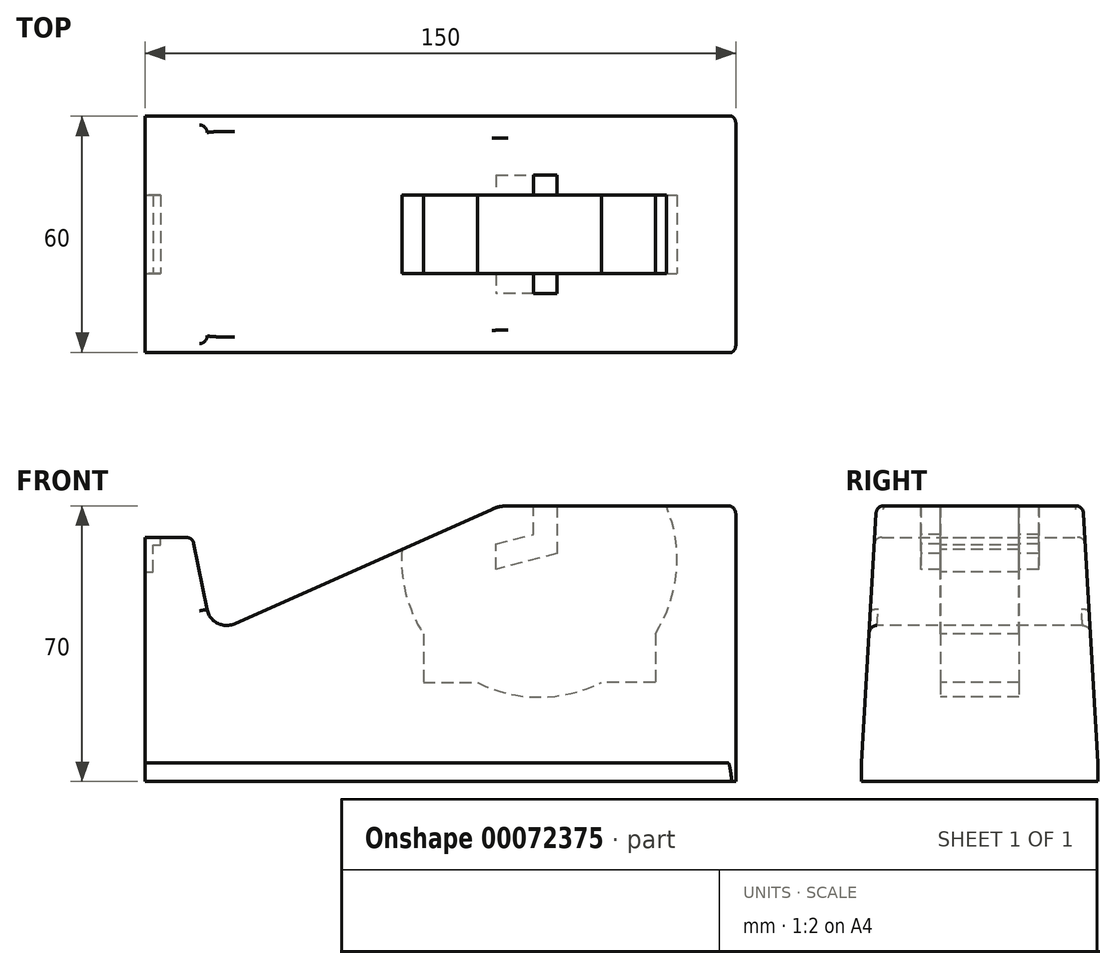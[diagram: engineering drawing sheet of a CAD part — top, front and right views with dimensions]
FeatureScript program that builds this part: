
annotation { "Feature Type Name" : "Feature", "Feature Type Description" : "" }
export const myFeature = defineFeature(function(context is Context, id is Id, definition is map)
    precondition{}
    {
        {
            var Q0;
            Q0=qCreatedBy(makeId("Front.planeOp"),FACE);
            var sketch = newSketch(context, id + "F0", { "sketchPlane" : qUnion([Q0])});
            skLineSegment(sketch, "E0", {"start": v(0, 0) * mm, "end": v(150, 0) * mm});
            skLineSegment(sketch, "E1", {"start": v(150, 0) * mm, "end": v(150, 70) * mm});
            skLineSegment(sketch, "E2", {"start": v(150, 70) * mm, "end": v(90, 70) * mm});
            skLineSegment(sketch, "E3", {"start": v(0, 62) * mm, "end": v(0, 0) * mm});
            skLineSegment(sketch, "E4", {"start": v(0, 62) * mm, "end": v(12, 62) * mm});
            skLineSegment(sketch, "E5", {"start": v(12, 62) * mm, "end": v(16.95, 37.5) * mm});
            skLineSegment(sketch, "E6", {"start": v(16.95, 37.5) * mm, "end": v(90, 70) * mm});
            skSolve(sketch);
        }
        {
            var Q0;
            Q0 = qSketchRegion(id + "F0", true);
            extrude(context, id + "F1", {"entities" : qUnion([Q0]), "depth" : 60 * mm, "symmetric" : true});
        }
        {
            var Q0;
            Q0=qCreatedBy(makeId("Front.planeOp"),FACE);
            var sketch = newSketch(context, id + "F2", { "sketchPlane" : qUnion([Q0])});
            skCircle(sketch, "E7", {"center": v(100.1, 56.39) * mm, "radius": 35 * mm});
            skLineSegment(sketch, "E8", {"start": v(0, 53.2) * mm, "end": v(1.94, 53.2) * mm});
            skLineSegment(sketch, "E9", {"start": v(1.94, 53.2) * mm, "end": v(1.94, 60) * mm});
            skLineSegment(sketch, "E10", {"start": v(1.94, 60) * mm, "end": v(3.89, 60) * mm});
            skLineSegment(sketch, "E11", {"start": v(3.89, 60) * mm, "end": v(3.89, 61.8) * mm});
            skLineSegment(sketch, "E12", {"start": v(3.89, 61.8) * mm, "end": v(0, 61.8) * mm});
            skLineSegment(sketch, "E13", {"start": v(0, 61.8) * mm, "end": v(0, 53.2) * mm});
            skLineSegment(sketch, "E14", {"start": v(70.65, 37.48) * mm, "end": v(70.65, 25.12) * mm});
            skLineSegment(sketch, "E15", {"start": v(129.55, 37.48) * mm, "end": v(129.55, 25.12) * mm});
            skLineSegment(sketch, "E16", {"start": v(70.65, 25.12) * mm, "end": v(84.36, 25.12) * mm});
            skLineSegment(sketch, "E17", {"start": v(129.55, 25.12) * mm, "end": v(115.84, 25.12) * mm});
            skSolve(sketch);
        }
        {
            var Q0;
            Q0 = qSketchRegion(id + "F2", true);
            extrude(context, id + "F3", {"entities" : qUnion([Q0]), "operationType" : NewBodyOperationType.REMOVE, "oppositeDirection" : true, "depth" : 20 * mm, "symmetric" : true});
        }
        {
            var Q0;
            Q0=qCreatedBy(makeId("Front.planeOp"),FACE);
            var sketch = newSketch(context, id + "F4", { "sketchPlane" : qUnion([Q0])});
            skLineSegment(sketch, "E18", {"start": v(104.65, 70.19) * mm, "end": v(104.65, 57.84) * mm});
            skLineSegment(sketch, "E19", {"start": v(104.65, 57.84) * mm, "end": v(89.14, 53.9) * mm});
            skLineSegment(sketch, "E20", {"start": v(89.14, 53.9) * mm, "end": v(89.14, 60.37) * mm});
            skLineSegment(sketch, "E21", {"start": v(89.14, 60.37) * mm, "end": v(98.65, 62.79) * mm});
            skLineSegment(sketch, "E22", {"start": v(98.65, 62.79) * mm, "end": v(98.65, 70.19) * mm});
            skLineSegment(sketch, "E23", {"start": v(104.65, 70.19) * mm, "end": v(98.65, 70.19) * mm});
            skSolve(sketch);
        }
        {
            var Q0;
            Q0 = qSketchRegion(id + "F4", true);
            extrude(context, id + "F5", {"entities" : qUnion([Q0]), "operationType" : NewBodyOperationType.REMOVE, "oppositeDirection" : true, "depth" : 30 * mm, "symmetric" : true});
        }
        {
            var Q0;
            Q0=qCreatedBy(makeId("Right.planeOp"),FACE);
            var sketch = newSketch(context, id + "F6", { "sketchPlane" : qUnion([Q0])});
            skLineSegment(sketch, "E24", {"start": v(30.27, 0) * mm, "end": v(25.6, 81.55) * mm});
            skLineSegment(sketch, "E25", {"start": v(25.6, 81.55) * mm, "end": v(45.78, 81.36) * mm});
            skLineSegment(sketch, "E26", {"start": v(45.78, 81.36) * mm, "end": v(30.27, 0) * mm});
            skLineSegment(sketch, "E27.MirrorCS", {"start": v(-25.6, 81.55) * mm, "end": v(-45.78, 81.36) * mm});
            skLineSegment(sketch, "E28.MirrorCS", {"start": v(-30.27, 0) * mm, "end": v(-25.6, 81.55) * mm});
            skLineSegment(sketch, "E29.MirrorCS", {"start": v(-45.78, 81.36) * mm, "end": v(-30.27, 0) * mm});
            skSolve(sketch);
        }
        {
            var Q0;
            Q0 = qSketchRegion(id + "F6", true);
            extrude(context, id + "F7", {"entities" : qUnion([Q0]), "operationType" : NewBodyOperationType.REMOVE, "endBound" : BoundingType.THROUGH_ALL, "depth" : 27.02 * mm});
        }
        {
            var Q0;
            Q0=makeQuery(id+"F1.opExtrude","SWEPT_EDGE",EDGE,{"disambiguationData":[OSD([sQuery(id+"F0.wireOp",EDGE,"E5"),sQuery(id+"F0.wireOp",EDGE,"E6")])]});
            fillet(context, id + "F8", {"entities" : qUnion([Q0]), "radius" : 5 * mm, "tangentPropagation" : true, "allowEdgeOverflow" : false});
        }
        {
            var Q0;
            Q0=makeQuery(id+"F1.opExtrude","SWEPT_EDGE",EDGE,{"disambiguationData":[OSD([sQuery(id+"F0.wireOp",EDGE,"E4"),sQuery(id+"F0.wireOp",EDGE,"E5")])]});
            var Q1;
            Q1=makeQuery(id+"F7.boolean.opBoolean","INTERSECT",EDGE,{"derivedFrom":[makeQuery(id+"F1.opExtrude","SWEPT_FACE",FACE,{"disambiguationData":[OSD([sQuery(id+"F0.wireOp",EDGE,"E6")])]}),makeQuery(id+"F7.opExtrude","SWEPT_FACE",FACE,{"disambiguationData":[OSD([sQuery(id+"F6.wireOp",EDGE,"E28.MirrorCS")])]})]});
            var Q2;
            Q2=makeQuery(id+"F7.boolean.opBoolean","INTERSECT",EDGE,{"derivedFrom":[makeQuery(id+"F1.opExtrude","SWEPT_FACE",FACE,{"disambiguationData":[OSD([sQuery(id+"F0.wireOp",EDGE,"E2")])]}),makeQuery(id+"F7.opExtrude","SWEPT_FACE",FACE,{"disambiguationData":[OSD([sQuery(id+"F6.wireOp",EDGE,"E28.MirrorCS")])]})]});
            var Q3;
            Q3=makeQuery(id+"F7.boolean.opBoolean","INTERSECT",EDGE,{"derivedFrom":[makeQuery(id+"F1.opExtrude","SWEPT_FACE",FACE,{"disambiguationData":[OSD([sQuery(id+"F0.wireOp",EDGE,"E1")])]}),makeQuery(id+"F7.opExtrude","SWEPT_FACE",FACE,{"disambiguationData":[OSD([sQuery(id+"F6.wireOp",EDGE,"E28.MirrorCS")])]})]});
            var Q4;
            Q4=makeQuery(id+"F1.opExtrude","SWEPT_EDGE",EDGE,{"disambiguationData":[OSD([sQuery(id+"F0.wireOp",EDGE,"E1"),sQuery(id+"F0.wireOp",EDGE,"E2")])]});
            var Q5;
            Q5=makeQuery(id+"F7.boolean.opBoolean","COPY",EDGE,{"derivedFrom":makeQuery(id+"F7.opExtrude","CAP_EDGE",EDGE,{"disambiguationData":[OSD([sQuery(id+"F6.wireOp",EDGE,"E28.MirrorCS")])],"isStart":true})});
            var Q6;
            Q6=makeQuery(id+"F7.boolean.opBoolean","INTERSECT",EDGE,{"derivedFrom":[makeQuery(id+"F1.opExtrude","SWEPT_FACE",FACE,{"disambiguationData":[OSD([sQuery(id+"F0.wireOp",EDGE,"E6")])]}),makeQuery(id+"F7.opExtrude","SWEPT_FACE",FACE,{"disambiguationData":[OSD([sQuery(id+"F6.wireOp",EDGE,"E24")])]})]});
            var Q7;
            Q7=makeQuery(id+"F7.boolean.opBoolean","INTERSECT",EDGE,{"derivedFrom":[makeQuery(id+"F1.opExtrude","SWEPT_FACE",FACE,{"disambiguationData":[OSD([sQuery(id+"F0.wireOp",EDGE,"E2")])]}),makeQuery(id+"F7.opExtrude","SWEPT_FACE",FACE,{"disambiguationData":[OSD([sQuery(id+"F6.wireOp",EDGE,"E24")])]})]});
            var Q8;
            Q8=makeQuery(id+"F7.boolean.opBoolean","COPY",EDGE,{"derivedFrom":makeQuery(id+"F7.opExtrude","CAP_EDGE",EDGE,{"disambiguationData":[OSD([sQuery(id+"F6.wireOp",EDGE,"E24")])],"isStart":true})});
            var Q9;
            Q9=makeQuery(id+"F7.boolean.opBoolean","INTERSECT",EDGE,{"derivedFrom":[makeQuery(id+"F1.opExtrude","SWEPT_FACE",FACE,{"disambiguationData":[OSD([sQuery(id+"F0.wireOp",EDGE,"E4")])]}),makeQuery(id+"F7.opExtrude","SWEPT_FACE",FACE,{"disambiguationData":[OSD([sQuery(id+"F6.wireOp",EDGE,"E24")])]})]});
            var Q10;
            Q10=makeQuery(id+"F7.boolean.opBoolean","INTERSECT",EDGE,{"derivedFrom":[makeQuery(id+"F1.opExtrude","SWEPT_FACE",FACE,{"disambiguationData":[OSD([sQuery(id+"F0.wireOp",EDGE,"E4")])]}),makeQuery(id+"F7.opExtrude","SWEPT_FACE",FACE,{"disambiguationData":[OSD([sQuery(id+"F6.wireOp",EDGE,"E28.MirrorCS")])]})]});
            var Q11;
            Q11=makeQuery(id+"F7.boolean.opBoolean","INTERSECT",EDGE,{"derivedFrom":[makeQuery(id+"F1.opExtrude","SWEPT_FACE",FACE,{"disambiguationData":[OSD([sQuery(id+"F0.wireOp",EDGE,"E1")])]}),makeQuery(id+"F7.opExtrude","SWEPT_FACE",FACE,{"disambiguationData":[OSD([sQuery(id+"F6.wireOp",EDGE,"E24")])]})]});
            fillet(context, id + "F9", {"entities" : qUnion([Q0, Q1, Q2, Q3, Q4, Q5, Q6, Q7, Q8, Q9, Q10, Q11]), "radius" : 2 * mm, "tangentPropagation" : true, "allowEdgeOverflow" : false});
        }
        {
            var Q0;
            {var subQ0=sQuery(id+"F0.wireOp",EDGE,"E6");var subQ1=sQuery(id+"F0.wireOp",EDGE,"E2");Q0=makeQuery(id+"F3.boolean.opBoolean","SPLIT",EDGE,{"disambiguationData":[TD([makeQuery(id+"F3.opExtrude","CAP_FACE",FACE,{"disambiguationData":[OSD([sQuery(id+"F2.wireOp",EDGE,"E7"),sQuery(id+"F2.wireOp",EDGE,"E14"),sQuery(id+"F2.wireOp",EDGE,"E15"),sQuery(id+"F2.wireOp",EDGE,"E16"),sQuery(id+"F2.wireOp",EDGE,"E17")])],"isStart":false})])],"derivedFrom":makeQuery(id+"F1.opExtrude","SWEPT_EDGE",EDGE,{"disambiguationData":[OSD([subQ1,subQ0])]})});}
            var Q1;
            {var subQ0=sQuery(id+"F0.wireOp",EDGE,"E6");var subQ1=sQuery(id+"F0.wireOp",EDGE,"E2");Q1=makeQuery(id+"F3.boolean.opBoolean","SPLIT",EDGE,{"disambiguationData":[TD([makeQuery(id+"F3.opExtrude","CAP_FACE",FACE,{"disambiguationData":[OSD([sQuery(id+"F2.wireOp",EDGE,"E7"),sQuery(id+"F2.wireOp",EDGE,"E14"),sQuery(id+"F2.wireOp",EDGE,"E15"),sQuery(id+"F2.wireOp",EDGE,"E16"),sQuery(id+"F2.wireOp",EDGE,"E17")])],"isStart":true})])],"derivedFrom":makeQuery(id+"F1.opExtrude","SWEPT_EDGE",EDGE,{"disambiguationData":[OSD([subQ1,subQ0])]})});}
            fillet(context, id + "F10", {"entities" : qUnion([Q0, Q1]), "radius" : 10 * mm, "tangentPropagation" : true, "allowEdgeOverflow" : false});
        }
    });
